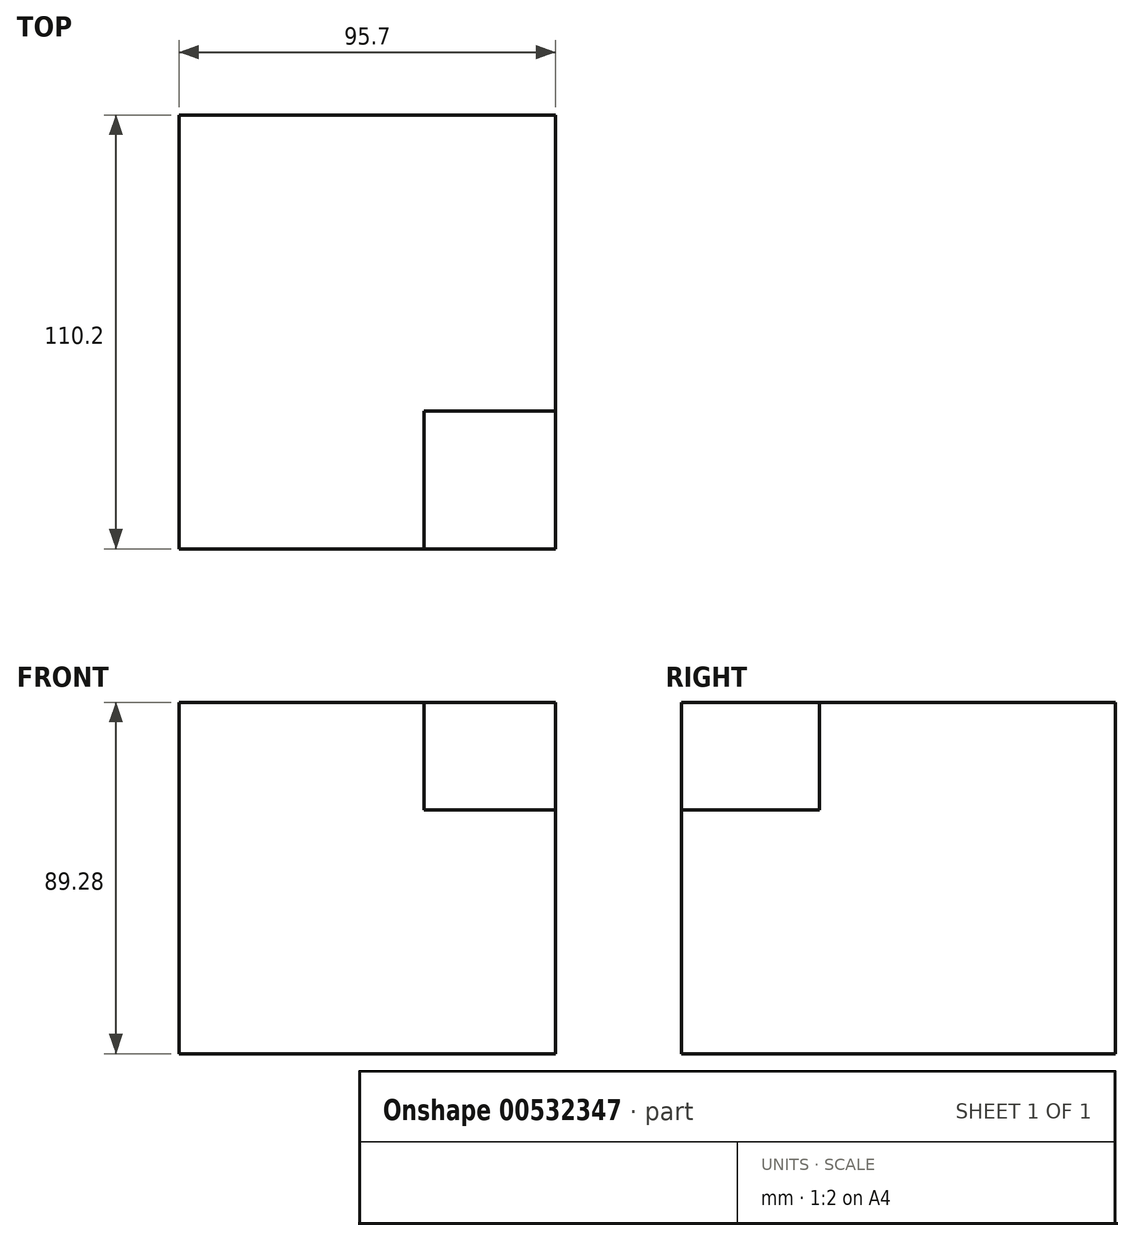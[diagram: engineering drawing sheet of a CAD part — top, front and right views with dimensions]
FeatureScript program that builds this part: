
annotation { "Feature Type Name" : "Feature", "Feature Type Description" : "" }
export const myFeature = defineFeature(function(context is Context, id is Id, definition is map)
    precondition{}
    {
        {
            var Q0;
            Q0=qCreatedBy(makeId("Front.planeOp"),FACE);
            var sketch = newSketch(context, id + "F0", { "sketchPlane" : qUnion([Q0])});
            skLineSegment(sketch, "E0.bottom", {"start": v(47.85, 44.64) * mm, "end": v(-47.85, 44.64) * mm});
            skLineSegment(sketch, "E0.top", {"start": v(47.85, -44.64) * mm, "end": v(-47.85, -44.64) * mm});
            skLineSegment(sketch, "E0.left", {"start": v(47.85, 44.64) * mm, "end": v(47.85, -44.64) * mm});
            skLineSegment(sketch, "E0.right", {"start": v(-47.85, 44.64) * mm, "end": v(-47.85, -44.64) * mm});
            skPoint(sketch, "E0.middle", {"position": v(0, 0) * mm});
            skSolve(sketch);
        }
        {
            var Q0;
            Q0=makeQuery(id+"F0.imprint","IMPRINT",FACE,{"disambiguationData":[TD([[makeQuery(id+"F0.imprint","IMPRINT",EDGE,{"derivedFrom":sQuery(id+"F0.wireOp",EDGE,"E0.bottom")}),1.0]])]});
            extrude(context, id + "F1", {"entities" : qUnion([Q0]), "endBound" : BoundingType.SYMMETRIC, "depth" : 110.2 * mm, "offsetDistance" : 25 * mm});
        }
        {
            var Q0;
            Q0=makeQuery(id+"F1.opExtrude","CAP_FACE",FACE,{"disambiguationData":[OSD([sQuery(id+"F0.wireOp",EDGE,"E0.bottom"),sQuery(id+"F0.wireOp",EDGE,"E0.top"),sQuery(id+"F0.wireOp",EDGE,"E0.left"),sQuery(id+"F0.wireOp",EDGE,"E0.right")])],"isStart":false});
            var sketch = newSketch(context, id + "F2", { "sketchPlane" : qUnion([Q0])});
            skLineSegment(sketch, "E1.bottom", {"start": v(47.85, 44.64) * mm, "end": v(14.4, 44.64) * mm});
            skLineSegment(sketch, "E1.top", {"start": v(47.85, 17.3) * mm, "end": v(14.4, 17.3) * mm});
            skLineSegment(sketch, "E1.left", {"start": v(47.85, 44.64) * mm, "end": v(47.85, 17.3) * mm});
            skLineSegment(sketch, "E1.right", {"start": v(14.4, 44.64) * mm, "end": v(14.4, 17.3) * mm});
            skSolve(sketch);
        }
        {
            var Q0;
            Q0=makeQuery(id+"F2.imprint","IMPRINT",FACE,{"disambiguationData":[TD([[makeQuery(id+"F2.imprint","IMPRINT",EDGE,{"derivedFrom":sQuery(id+"F2.wireOp",EDGE,"E1.bottom")}),1.0]])]});
            extrude(context, id + "F3", {"entities" : qUnion([Q0]), "operationType" : NewBodyOperationType.REMOVE, "oppositeDirection" : true, "depth" : 35 * mm, "offsetDistance" : 25 * mm});
        }
    });
